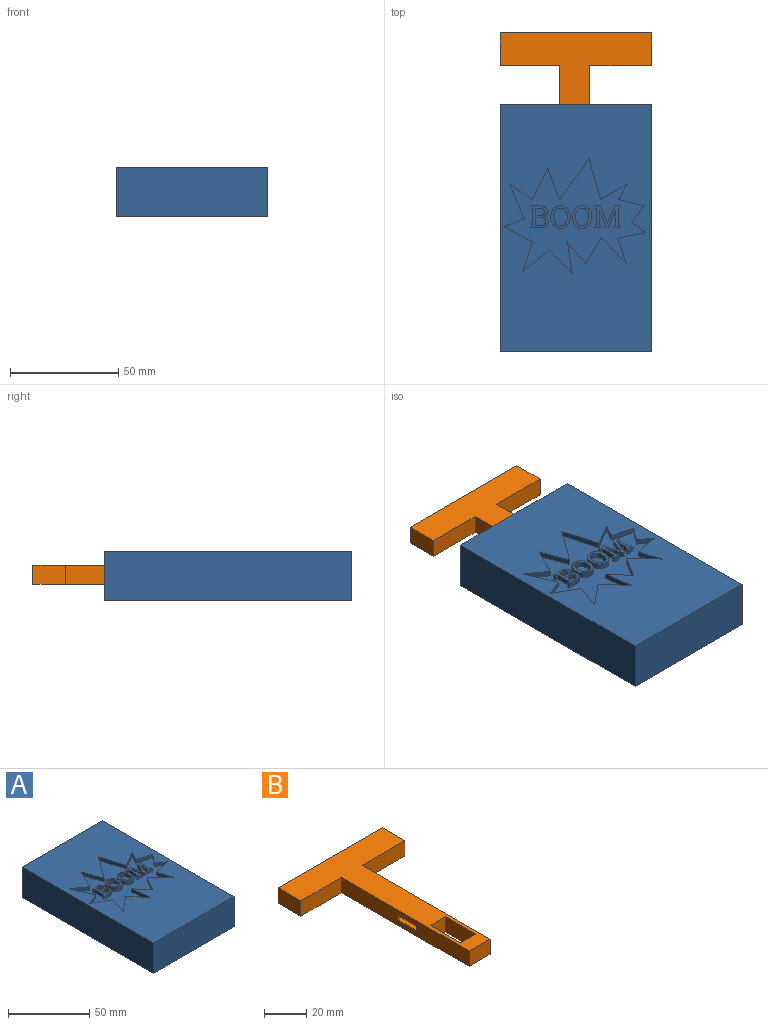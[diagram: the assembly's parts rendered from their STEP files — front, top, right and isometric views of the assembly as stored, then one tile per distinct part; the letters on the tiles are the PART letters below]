
ASSEMBLY  parts=2 mates=1
PART A: 160 faces, bbox 69.9x114.3x22.9 mm
  f0: plane 114.3x69.85mm, normal (0,0,1), area 6341.6mm2, adj f18,f19,f20,f23,f91,f92,f93,f94
  f1: plane 25.4x15.24mm, normal (0,0,1), area 316mm2, adj f3,f4,f5,f9,f10,f11,f12,f24
  f2: plane 25.4x15.24mm, normal (0,0,1), area 316mm2, adj f6,f7,f8,f14,f15,f16,f17,f21
  f3: plane 5.08x4.78mm, normal (0,-1,0), area 24.3mm2, adj f1,f4,f24,f25
  f4: plane 5.08x5.08mm, normal (-1,0,0), area 25.8mm2, adj f1,f3,f5,f25
  f5: cylinder r=3.97mm len=7.94mm, axis (0,0,-1), area 100.6mm2, adj f1,f4,f24,f25
  f6: plane 5.08x5.08mm, normal (-1,0,0), area 25.8mm2, adj f2,f7,f21,f25
  f7: cylinder r=3.97mm len=7.94mm, axis (0,0,-1), area 100.6mm2, adj f2,f6,f8,f25
  f8: plane 5.08x5.08mm, normal (1,0,0), area 25.8mm2, adj f2,f7,f21,f25
  f9: plane 25.4x5.08mm, normal (-1,0,0), area 129mm2, adj f1,f10,f12,f25
  f10: plane 15.24x5.08mm, normal (0,-1,0), area 77.4mm2, adj f1,f9,f11,f25
  f11: plane 25.4x5.08mm, normal (1,0,0), area 129mm2, adj f1,f10,f12,f25
  f12: plane 49.53x17.78mm, normal (0,-1,0), area 648.4mm2, adj f1,f9,f11,f13,f22,f25,f26,f27
  f13: plane 93.98x17.78mm, normal (-1,0,0), area 1671mm2, adj f12,f17,f25,f26
  f14: plane 25.4x5.08mm, normal (1,0,0), area 129mm2, adj f2,f15,f17,f25
  f15: plane 15.24x5.08mm, normal (0,1,0), area 77.4mm2, adj f2,f14,f16,f25
  f16: plane 25.4x5.08mm, normal (-1,0,0), area 129mm2, adj f2,f15,f17,f25
  f17: plane 49.53x17.78mm, normal (0,1,0), area 803.2mm2, adj f2,f13,f14,f16,f22,f25,f26
  f18: plane 114.3x22.86mm, normal (-1,0,0), area 2612.9mm2, adj f0,f19,f23,f25
  f19: plane 69.85x22.86mm, normal (0,-1,0), area 1596.8mm2, adj f0,f18,f20,f25
  f20: plane 114.3x22.86mm, normal (1,0,0), area 2612.9mm2, adj f0,f19,f23,f25
  f21: plane 5.08x4.78mm, normal (0,-1,0), area 24.3mm2, adj f2,f6,f8,f25
  f22: plane 93.98x17.78mm, normal (1,0,0), area 1671mm2, adj f12,f17,f25,f26
  f23: plane 69.85x22.86mm, normal (0,1,0), area 1441.9mm2, adj f0,f18,f20,f25,f26,f27,f28,f29
  f24: plane 5.08x5.08mm, normal (1,0,0), area 25.8mm2, adj f1,f3,f5,f25
  f25: plane 114.3x69.85mm, normal (0,0,-1), area 3960.9mm2, adj f3,f4,f5,f6,f7,f8,f9,f10
  f26: plane 104.14x49.53mm, normal (0,0,-1), area 4809.7mm2, adj f12,f13,f17,f22,f23,f27,f29
  f27: plane 10.16x10.16mm, normal (-1,0,0), area 103.2mm2, adj f12,f23,f26,f28
  f28: plane 15.24x10.16mm, normal (0,0,1), area 154.8mm2, adj f12,f23,f27,f29
  f29: plane 10.16x10.16mm, normal (1,0,0), area 103.2mm2, adj f12,f23,f26,f28
  f30: plane 2.94x2.54mm, normal (-1,0,0), area 7.5mm2, adj f31,f116,f117,f121
  f31: plane 4.11x2.54mm, normal (-1,0.03,0), area 10.4mm2, adj f30,f32,f117,f121
  f32: plane 2.54x0.04mm, normal (-0.18,-0.98,0), area 0.1mm2, adj f31,f33,f117,f121
  f33: plane 8.13x3.28mm, normal (0.93,-0.37,0), area 22.3mm2, adj f32,f34,f117,f121
  f34: plane 2.54x0.91mm, normal (0,-1,0), area 2.3mm2, adj f33,f35,f117,f121
  f35: plane 8.13x3.28mm, normal (-0.93,-0.37,0), area 22.3mm2, adj f34,f36,f117,f121
  f36: plane 2.54x0.04mm, normal (0.18,-0.98,0), area 0.1mm2, adj f35,f37,f117,f121
  f37: plane 4.11x2.54mm, normal (1,0.03,0), area 10.4mm2, adj f36,f38,f117,f121
  f38: plane 2.94x2.54mm, normal (1,0,0), area 7.5mm2, adj f37,f39,f117,f121
  f39: plane 2.54x1.14mm, normal (0.17,0.99,0), area 2.9mm2, adj f38,f40,f117,f121
  f40: plane 2.54x0.88mm, normal (1,0,0), area 2.2mm2, adj f39,f41,f117,f121
  f41: plane 3.64x2.54mm, normal (0,-1,0), area 9.3mm2, adj f40,f42,f117,f121
  f42: plane 2.54x0.88mm, normal (-1,0,0), area 2.2mm2, adj f41,f43,f117,f121
  f43: plane 2.54x1.14mm, normal (-0.17,0.99,0), area 2.9mm2, adj f42,f44,f117,f121
  f44: plane 7.99x2.54mm, normal (-1,0,0), area 20.3mm2, adj f43,f45,f117,f121
  f45: plane 2.54x1.14mm, normal (-0.17,-0.99,0), area 2.9mm2, adj f44,f46,f117,f121
  f46: plane 2.54x0.89mm, normal (-1,0,0), area 2.2mm2, adj f45,f47,f117,f121
  f47: plane 2.89x2.54mm, normal (0,1,0), area 7.3mm2, adj f46,f48,f117,f121
  f48: plane 8.24x3.23mm, normal (0.93,0.37,0), area 22.5mm2, adj f47,f49,f117,f121
  f49: plane 2.54x0.04mm, normal (0,1,0), area 0.1mm2, adj f48,f50,f117,f121
  f50: plane 8.24x3.22mm, normal (-0.93,0.36,0), area 22.5mm2, adj f49,f51,f117,f121
  f51: plane 2.9x2.54mm, normal (0,1,0), area 7.4mm2, adj f50,f52,f117,f121
  f52: plane 2.54x0.89mm, normal (1,0,0), area 2.2mm2, adj f51,f53,f117,f121
  f53: plane 2.54x1.14mm, normal (0.17,-0.99,0), area 2.9mm2, adj f52,f54,f117,f121
  f54: plane 7.99x2.54mm, normal (1,0,0), area 20.3mm2, adj f53,f55,f117,f121
  f55: plane 2.54x1.14mm, normal (0.17,0.99,0), area 2.9mm2, adj f54,f56,f117,f121
  f56: plane 2.54x0.88mm, normal (1,0,0), area 2.2mm2, adj f55,f57,f117,f121
  f57: plane 3.64x2.54mm, normal (0,-1,0), area 9.3mm2, adj f56,f58,f117,f121
  f58: plane 2.54x0.88mm, normal (-1,0,0), area 2.2mm2, adj f57,f116,f117,f121
  f59: extruded ~3.68x2.54mm, area 10.1mm2, adj f60,f112,f117,f120
  f60: plane 2.54x0.15mm, normal (1,0,0), area 0.4mm2, adj f59,f61,f117,f120
  f61: extruded ~3.68x2.54mm, area 10.1mm2, adj f60,f62,f117,f120
  f62: extruded ~3.29x2.54mm, area 9.5mm2, adj f61,f63,f117,f120
  f63: extruded ~3.19x2.54mm, area 9.2mm2, adj f62,f64,f117,f120
  f64: extruded ~3.68x2.54mm, area 10.1mm2, adj f63,f65,f117,f120
  f65: plane 2.54x0.15mm, normal (-1,0,0), area 0.4mm2, adj f64,f66,f117,f120
  f66: extruded ~3.68x2.54mm, area 10.1mm2, adj f65,f67,f117,f120
  f67: extruded ~3.19x2.54mm, area 9.2mm2, adj f66,f112,f117,f120
  f68: extruded ~3.68x2.54mm, area 10.1mm2, adj f69,f113,f117,f119
  f69: plane 2.54x0.15mm, normal (1,0,0), area 0.4mm2, adj f68,f70,f117,f119
  f70: extruded ~3.68x2.54mm, area 10.1mm2, adj f69,f71,f117,f119
  f71: extruded ~3.29x2.54mm, area 9.5mm2, adj f70,f72,f117,f119
  f72: extruded ~3.19x2.54mm, area 9.2mm2, adj f71,f73,f117,f119
  f73: extruded ~3.68x2.54mm, area 10.1mm2, adj f72,f74,f117,f119
  f74: plane 2.54x0.15mm, normal (-1,0,0), area 0.4mm2, adj f73,f75,f117,f119
  f75: extruded ~3.68x2.54mm, area 10.1mm2, adj f74,f76,f117,f119
  f76: extruded ~3.19x2.54mm, area 9.2mm2, adj f75,f113,f117,f119
  f77: plane 4.45x2.54mm, normal (0,1,0), area 11.3mm2, adj f78,f114,f117,f118
  f78: extruded ~2.54x2.48mm, area 6.7mm2, adj f77,f79,f117,f118
  f79: extruded ~2.54x2.06mm, area 5.9mm2, adj f78,f80,f117,f118
  f80: extruded ~2.54x1.21mm, area 3.3mm2, adj f79,f81,f117,f118
  f81: extruded ~2.54x1.13mm, area 3.6mm2, adj f80,f82,f117,f118
  f82: extruded ~2.54x1.44mm, area 4.4mm2, adj f81,f83,f117,f118
  f83: extruded ~2.54x1.64mm, area 4.5mm2, adj f82,f84,f117,f118
  f84: extruded ~2.54x2.13mm, area 6.1mm2, adj f83,f85,f117,f118
  f85: extruded ~2.54x2.45mm, area 6.6mm2, adj f84,f86,f117,f118
  f86: plane 4.88x2.54mm, normal (0,-1,0), area 12.4mm2, adj f85,f87,f117,f118
  f87: plane 2.54x0.88mm, normal (-1,0,0), area 2.2mm2, adj f86,f88,f117,f118
  f88: plane 2.54x1.14mm, normal (-0.17,0.99,0), area 2.9mm2, adj f87,f89,f117,f118
  f89: plane 7.99x2.54mm, normal (-1,0,0), area 20.3mm2, adj f88,f90,f117,f118
  f90: plane 2.54x1.14mm, normal (-0.17,-0.99,0), area 2.9mm2, adj f89,f114,f117,f118
  f91: plane 11.08x10.5mm, normal (0.73,0.69,0), area 38.8mm2, adj f0,f92,f115,f117
  f92: plane 14.68x2.54mm, normal (-0.99,-0.14,0), area 37.7mm2, adj f0,f91,f93,f117
  f93: plane 10.09x8.4mm, normal (0.77,0.64,0), area 33.4mm2, adj f0,f92,f94,f117
  f94: plane 12.03x7.26mm, normal (-0.86,0.52,0), area 35.7mm2, adj f0,f93,f95,f117
  f95: plane 12.03x11.46mm, normal (0.72,0.69,0), area 42.2mm2, adj f0,f94,f96,f117
  f96: plane 11.84x3.82mm, normal (-0.95,-0.31,0), area 31.6mm2, adj f0,f95,f97,f117
  f97: plane 12.83x2.58mm, normal (-0.2,0.98,0), area 33.2mm2, adj f0,f96,f98,f117
  f98: plane 6.53x5.06mm, normal (-0.61,-0.79,0), area 21mm2, adj f0,f97,f99,f117
  f99: plane 7.4x5.73mm, normal (-0.79,0.61,0), area 23.8mm2, adj f0,f98,f100,f117
  f100: plane 11.65x2.92mm, normal (-0.24,-0.97,0), area 30.5mm2, adj f0,f99,f101,f117
  f101: plane 7.04x3.82mm, normal (-0.88,0.48,0), area 20.3mm2, adj f0,f100,f102,f117
  f102: plane 12.22x7.04mm, normal (0.5,-0.87,0), area 35.8mm2, adj f0,f101,f103,f117
  f103: plane 18.71x5.35mm, normal (-0.96,-0.27,0), area 49.4mm2, adj f0,f102,f104,f117
  f104: plane 18.71x13.75mm, normal (0.81,-0.59,0), area 59mm2, adj f0,f103,f105,f117
  f105: plane 14.51x5.35mm, normal (-0.94,-0.35,0), area 39.3mm2, adj f0,f104,f106,f117
  f106: plane 14.51x7.26mm, normal (0.89,-0.45,0), area 41.2mm2, adj f0,f105,f107,f117
  f107: plane 10.36x7.04mm, normal (-0.56,-0.83,0), area 31.8mm2, adj f0,f106,f108,f117
  f108: plane 15.82x6.73mm, normal (0.92,0.39,0), area 43.7mm2, adj f0,f107,f109,f117
  f109: plane 8.98x3.82mm, normal (0.39,-0.92,0), area 24.8mm2, adj f0,f108,f110,f117
  f110: plane 12.6x7.09mm, normal (0.49,0.87,0), area 36.7mm2, adj f0,f109,f111,f117
  f111: plane 13.53x4.2mm, normal (0.96,-0.3,0), area 36mm2, adj f0,f110,f115,f117
  f112: extruded ~3.29x2.54mm, area 9.5mm2, adj f59,f67,f117,f120
  f113: extruded ~3.29x2.54mm, area 9.5mm2, adj f68,f76,f117,f119
  f114: plane 2.54x0.89mm, normal (-1,0,0), area 2.2mm2, adj f77,f90,f117,f118
  f115: plane 12.22x9.93mm, normal (-0.63,0.78,0), area 40mm2, adj f0,f91,f111,f117
  f116: plane 2.54x1.14mm, normal (-0.17,0.99,0), area 2.9mm2, adj f30,f58,f117,f121
  f117: plane 65.15x53.09mm, normal (0,0,1), area 1369mm2, adj f30,f31,f32,f33,f34,f35,f36,f37
  f118: plane 10.15x8.24mm, normal (0,0,1), area 40.4mm2, adj f77,f78,f79,f80,f81,f82,f83,f84
  f119: plane 10.44x8.98mm, normal (0,0,1), area 33.7mm2, adj f68,f69,f70,f71,f72,f73,f74,f75
  f120: plane 10.44x8.98mm, normal (0,0,1), area 33.7mm2, adj f59,f60,f61,f62,f63,f64,f65,f66
  f121: plane 12.29x10.15mm, normal (0,0,1), area 55.8mm2, adj f30,f31,f32,f33,f34,f35,f36,f37
  f122: extruded ~2.91x2.54mm, area 7.8mm2, adj f120,f123,f131,f132
  f123: plane 2.54x0.16mm, normal (-1,0,0), area 0.4mm2, adj f120,f122,f124,f132
  f124: extruded ~2.89x2.54mm, area 7.8mm2, adj f120,f123,f125,f132
  f125: extruded ~2.54x2.34mm, area 6.9mm2, adj f120,f124,f126,f132
  f126: extruded ~2.54x2.24mm, area 6.6mm2, adj f120,f125,f127,f132
  f127: extruded ~2.88x2.54mm, area 7.7mm2, adj f120,f126,f128,f132
  f128: plane 2.54x0.16mm, normal (1,0,0), area 0.4mm2, adj f120,f127,f129,f132
  f129: extruded ~2.9x2.54mm, area 7.8mm2, adj f120,f128,f130,f132
  f130: extruded ~2.54x2.24mm, area 6.6mm2, adj f120,f129,f131,f132
  f131: extruded ~2.54x2.35mm, area 6.9mm2, adj f120,f122,f130,f132
  f132: plane 8.19x6.23mm, normal (0,0,1), area 41.6mm2, adj f122,f123,f124,f125,f126,f127,f128,f129
  f133: extruded ~2.91x2.54mm, area 7.8mm2, adj f119,f134,f142,f143
  f134: plane 2.54x0.16mm, normal (-1,0,0), area 0.4mm2, adj f119,f133,f135,f143
  f135: extruded ~2.89x2.54mm, area 7.8mm2, adj f119,f134,f136,f143
  f136: extruded ~2.54x2.34mm, area 6.9mm2, adj f119,f135,f137,f143
  f137: extruded ~2.54x2.24mm, area 6.6mm2, adj f119,f136,f138,f143
  f138: extruded ~2.88x2.54mm, area 7.7mm2, adj f119,f137,f139,f143
  f139: plane 2.54x0.16mm, normal (1,0,0), area 0.4mm2, adj f119,f138,f140,f143
  f140: extruded ~2.9x2.54mm, area 7.8mm2, adj f119,f139,f141,f143
  f141: extruded ~2.54x2.24mm, area 6.6mm2, adj f119,f140,f142,f143
  f142: extruded ~2.54x2.35mm, area 6.9mm2, adj f119,f133,f141,f143
  f143: plane 8.19x6.23mm, normal (0,0,1), area 41.6mm2, adj f133,f134,f135,f136,f137,f138,f139,f140
  f144: extruded ~2.54x1.33mm, area 3.7mm2, adj f118,f145,f150,f151
  f145: plane 2.58x2.54mm, normal (0,-1,0), area 6.5mm2, adj f118,f144,f146,f151
  f146: plane 3.69x2.54mm, normal (1,0,0), area 9.4mm2, adj f118,f145,f147,f151
  f147: plane 2.54x2.37mm, normal (0,1,0), area 6mm2, adj f118,f146,f148,f151
  f148: extruded ~2.54x1.46mm, area 4mm2, adj f118,f147,f149,f151
  f149: extruded ~2.54x1.31mm, area 3.7mm2, adj f118,f148,f150,f151
  f150: extruded ~2.54x1.4mm, area 3.8mm2, adj f118,f144,f149,f151
  f151: plane 4.35x3.69mm, normal (0,0,1), area 14.8mm2, adj f144,f145,f146,f147,f148,f149,f150
  f152: plane 2.54x1.94mm, normal (0,-1,0), area 4.9mm2, adj f118,f153,f158,f159
  f153: plane 3.23x2.54mm, normal (1,0,0), area 8.2mm2, adj f118,f152,f154,f159
  f154: plane 2.54x2.29mm, normal (0,1,0), area 5.8mm2, adj f118,f153,f155,f159
  f155: extruded ~2.54x1.2mm, area 3.3mm2, adj f118,f154,f156,f159
  f156: extruded ~2.54x1.16mm, area 3.3mm2, adj f118,f155,f157,f159
  f157: extruded ~2.54x1.23mm, area 3.5mm2, adj f118,f156,f158,f159
  f158: extruded ~2.54x1.49mm, area 4mm2, adj f118,f152,f157,f159
  f159: plane 3.94x3.23mm, normal (0,0,1), area 11.7mm2, adj f152,f153,f154,f155,f156,f157,f158
PART B: 18 faces, bbox 69.9x100.8x8.9 mm
  f0: plane 100.84x69.85mm, normal (0,0,-1), area 2053.9mm2, adj f1,f3,f4,f5,f6,f7,f8,f9
  f1: plane 85.6x8.89mm, normal (1,0,0), area 728.7mm2, adj f0,f2,f4,f9,f14,f15,f16,f17
  f2: plane 100.84x69.85mm, normal (0,0,1), area 2053.9mm2, adj f1,f3,f4,f5,f6,f7,f8,f9
  f3: plane 85.6x8.89mm, normal (-1,0,0), area 728.7mm2, adj f0,f2,f4,f13,f14,f15,f16,f17
  f4: plane 13.97x8.89mm, normal (0,-1,0), area 124.2mm2, adj f0,f1,f2,f3
  f5: plane 20.32x8.89mm, normal (-1,0,0), area 180.6mm2, adj f0,f2,f6,f8
  f6: plane 10.16x8.89mm, normal (0,-1,0), area 90.3mm2, adj f0,f2,f5,f7
  f7: plane 20.32x8.89mm, normal (1,0,0), area 180.6mm2, adj f0,f2,f6,f8
  f8: plane 10.16x8.89mm, normal (0,1,0), area 90.3mm2, adj f0,f2,f5,f7
  f9: plane 28.58x8.89mm, normal (0,-1,0), area 254mm2, adj f0,f1,f2,f11
  f10: plane 15.24x8.89mm, normal (-1,0,0), area 135.5mm2, adj f0,f2,f12,f13
  f11: plane 15.24x8.89mm, normal (1,0,0), area 135.5mm2, adj f0,f2,f9,f12
  f12: plane 69.85x8.89mm, normal (0,1,0), area 621mm2, adj f0,f2,f10,f11
  f13: plane 27.31x8.89mm, normal (0,-1,0), area 242.7mm2, adj f0,f2,f3,f10
  f14: plane 13.97x2.54mm, normal (0,-1,0), area 35.5mm2, adj f1,f3,f15,f17
  f15: plane 13.97x12.7mm, normal (0,0,1), area 177.4mm2, adj f1,f3,f14,f16
  f16: plane 13.97x2.54mm, normal (0,1,0), area 35.5mm2, adj f1,f3,f15,f17
  f17: plane 13.97x12.7mm, normal (0,0,-1), area 177.4mm2, adj f1,f3,f14,f16
PLACE A t=(-10.94,-3.34,-3.33)mm fixed
PLACE B t=(62.68,12.92,-7.36)mm
MATE slider A.f23 <-> B.f13  axis (0,1,0) through (-18.56,60.47,4.29)mm
